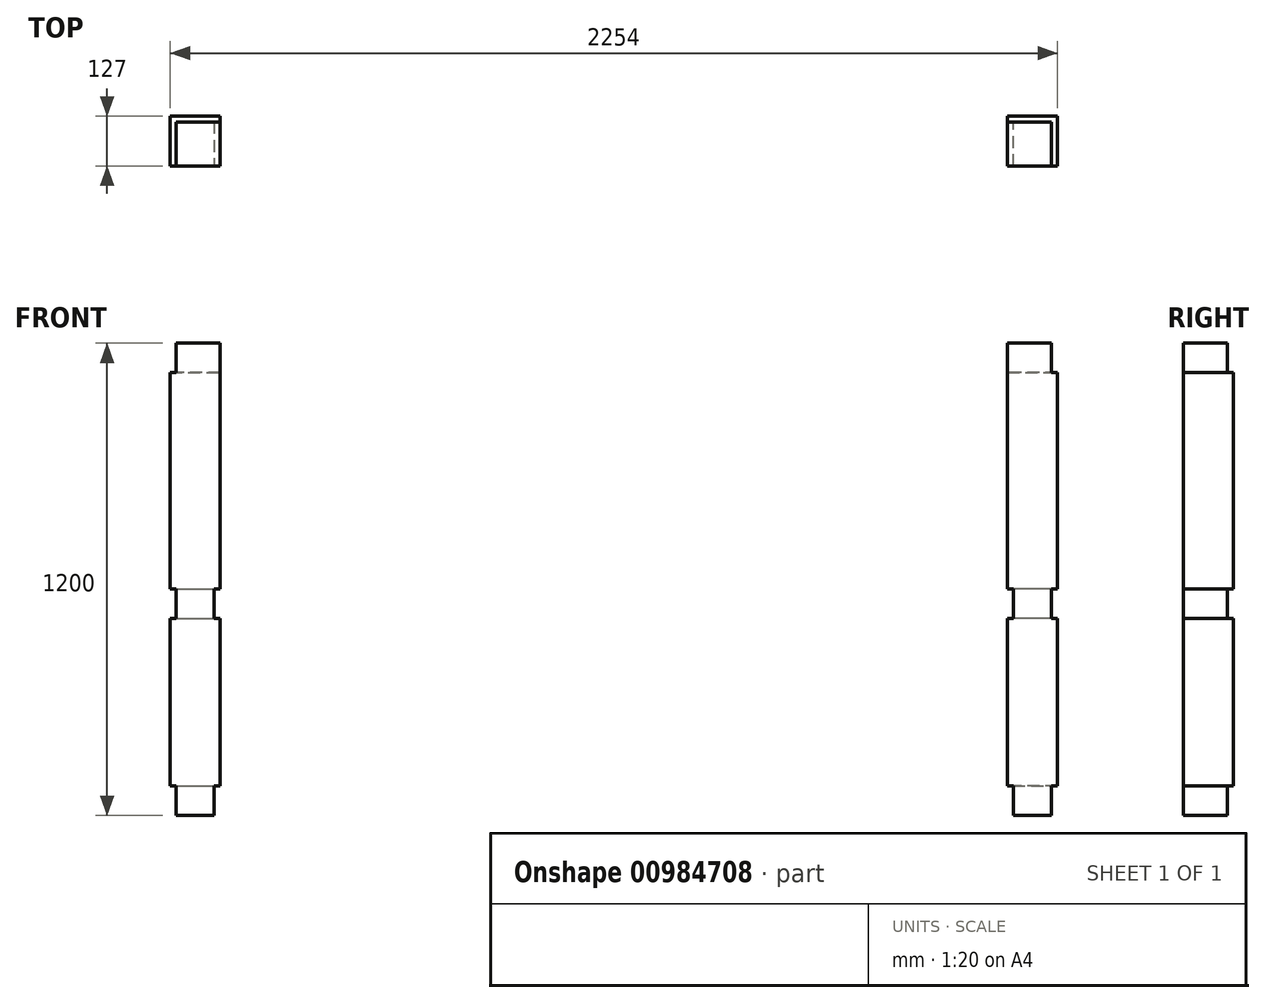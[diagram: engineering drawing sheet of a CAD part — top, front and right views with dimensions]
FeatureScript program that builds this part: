
annotation { "Feature Type Name" : "Feature", "Feature Type Description" : "" }
export const myFeature = defineFeature(function(context is Context, id is Id, definition is map)
    precondition{}
    {
        {
            var Q0;
            Q0=qCreatedBy(makeId("Top.planeOp"),FACE);
            var sketch = newSketch(context, id + "F0", { "sketchPlane" : qUnion([Q0])});
            skLineSegment(sketch, "E0.bottom", {"start": v(0, 0) * mm, "end": v(127, 0) * mm});
            skLineSegment(sketch, "E0.top", {"start": v(0, 127) * mm, "end": v(127, 127) * mm});
            skLineSegment(sketch, "E0.left", {"start": v(0, 0) * mm, "end": v(0, 127) * mm});
            skLineSegment(sketch, "E0.right", {"start": v(127, 0) * mm, "end": v(127, 127) * mm});
            skSolve(sketch);
        }
        {
            var Q0;
            Q0=qSketchRegion(id+"F0",true);
            extrude(context, id + "F1", {"entities" : qUnion([Q0]), "depth" : 1200 * mm, "offsetDistance" : 25.4 * mm});
        }
        {
            var Q0;
            Q0=makeQuery(id+"F1.opExtrude","CAP_FACE",FACE,{"disambiguationData":[OSD([sQuery(id+"F0.wireOp",EDGE,"E0.bottom"),sQuery(id+"F0.wireOp",EDGE,"E0.top"),sQuery(id+"F0.wireOp",EDGE,"E0.left"),sQuery(id+"F0.wireOp",EDGE,"E0.right")])],"isStart":false});
            var sketch = newSketch(context, id + "F2", { "sketchPlane" : qUnion([Q0])});
            skLineSegment(sketch, "E1", {"start": v(0, 0) * mm, "end": v(0, 127) * mm});
            skLineSegment(sketch, "E2", {"start": v(0, 127) * mm, "end": v(127, 127) * mm});
            skLineSegment(sketch, "E3", {"start": v(127, 127) * mm, "end": v(127, 112) * mm});
            skLineSegment(sketch, "E4", {"start": v(127, 112) * mm, "end": v(15, 112) * mm});
            skLineSegment(sketch, "E5", {"start": v(15, 112) * mm, "end": v(15, 0) * mm});
            skLineSegment(sketch, "E6", {"start": v(15, 0) * mm, "end": v(0, 0) * mm});
            skSolve(sketch);
        }
        {
            var Q0;
            Q0=qSketchRegion(id+"F2",true);
            extrude(context, id + "F3", {"entities" : qUnion([Q0]), "operationType" : NewBodyOperationType.REMOVE, "oppositeDirection" : true, "depth" : 75 * mm, "offsetDistance" : 25.4 * mm});
        }
        {
            var Q0;
            Q0=makeQuery(id+"F1.opExtrude","CAP_FACE",FACE,{"disambiguationData":[OSD([sQuery(id+"F0.wireOp",EDGE,"E0.bottom"),sQuery(id+"F0.wireOp",EDGE,"E0.top"),sQuery(id+"F0.wireOp",EDGE,"E0.left"),sQuery(id+"F0.wireOp",EDGE,"E0.right")])],"isStart":true});
            var sketch = newSketch(context, id + "F4", { "sketchPlane" : qUnion([Q0])});
            skLineSegment(sketch, "E7", {"start": v(0, 0) * mm, "end": v(15, 0) * mm});
            skLineSegment(sketch, "E8", {"start": v(15, 0) * mm, "end": v(15, -112) * mm});
            skLineSegment(sketch, "E9", {"start": v(15, -112) * mm, "end": v(112, -112) * mm});
            skLineSegment(sketch, "E10", {"start": v(112, -112) * mm, "end": v(112, 0) * mm});
            skLineSegment(sketch, "E11", {"start": v(112, 0) * mm, "end": v(127, 0) * mm});
            skLineSegment(sketch, "E12", {"start": v(127, 0) * mm, "end": v(127, -127) * mm});
            skLineSegment(sketch, "E13", {"start": v(127, -127) * mm, "end": v(0, -127) * mm});
            skLineSegment(sketch, "E14", {"start": v(0, -127) * mm, "end": v(0, 0) * mm});
            skSolve(sketch);
        }
        {
            var Q0;
            Q0=qSketchRegion(id+"F4",true);
            extrude(context, id + "F5", {"entities" : qUnion([Q0]), "operationType" : NewBodyOperationType.REMOVE, "oppositeDirection" : true, "depth" : 575 * mm, "offsetDistance" : 25.4 * mm, "hasSecondDirection" : true, "secondDirectionOppositeDirection" : true, "secondDirectionDepth" : 500 * mm});
        }
        {
            var Q0;
            Q0=qCreatedBy(makeId("Right.planeOp"),FACE);
            cPlane(context, id + "F6", {"entities" : qUnion([Q0]), "cplaneType" : CPlaneType.OFFSET, "offset" : 1127 * mm, "width" : 152.4 * mm, "height" : 152.4 * mm});
        }
        {
            var Q0;
            Q0=makeQuery(id+"F1.opExtrude","SWEPT_BODY",BODY,{"disambiguationData":[OSD([sQuery(id+"F0.wireOp",EDGE,"E0.bottom"),sQuery(id+"F0.wireOp",EDGE,"E0.top"),sQuery(id+"F0.wireOp",EDGE,"E0.left"),sQuery(id+"F0.wireOp",EDGE,"E0.right")])]});
            var Q1;
            Q1=qCreatedBy(id+"F6.planeOp",FACE);
            mirror(context, id + "F7", {"entities" : qUnion([Q0]), "mirrorPlane" : qUnion([Q1])});
        }
        {
            var Q0;
            Q0=makeQuery(id+"F7.opPattern","COPY",FACE,{"derivedFrom":makeQuery(id+"F1.opExtrude","CAP_FACE",FACE,{"disambiguationData":[OSD([sQuery(id+"F0.wireOp",EDGE,"E0.bottom"),sQuery(id+"F0.wireOp",EDGE,"E0.top"),sQuery(id+"F0.wireOp",EDGE,"E0.left"),sQuery(id+"F0.wireOp",EDGE,"E0.right")])],"isStart":true}),"instanceName":"1"});
            var sketch = newSketch(context, id + "F8", { "sketchPlane" : qUnion([Q0])});
            skLineSegment(sketch, "E15", {"start": v(2254, 0) * mm, "end": v(2254, -127) * mm});
            skLineSegment(sketch, "E16", {"start": v(2254, -127) * mm, "end": v(2127, -127) * mm});
            skLineSegment(sketch, "E17", {"start": v(2127, -127) * mm, "end": v(2127, 0) * mm});
            skLineSegment(sketch, "E18", {"start": v(2127, 0) * mm, "end": v(2142, 0) * mm});
            skLineSegment(sketch, "E19", {"start": v(2142, 0) * mm, "end": v(2142, -112) * mm});
            skLineSegment(sketch, "E20", {"start": v(2142, -112) * mm, "end": v(2239, -112) * mm});
            skLineSegment(sketch, "E21", {"start": v(2239, -112) * mm, "end": v(2239, 0) * mm});
            skLineSegment(sketch, "E22", {"start": v(2239, 0) * mm, "end": v(2254, 0) * mm});
            skSolve(sketch);
        }
        {
            var Q0;
            Q0=makeQuery(id+"F8.imprint","IMPRINT",FACE,{"disambiguationData":[TD([[makeQuery(id+"F8.imprint","IMPRINT",EDGE,{"derivedFrom":sQuery(id+"F8.wireOp",EDGE,"E15")}),-1.0]])]});
            extrude(context, id + "F9", {"entities" : qUnion([Q0]), "operationType" : NewBodyOperationType.REMOVE, "oppositeDirection" : true, "depth" : 75 * mm, "offsetDistance" : 25.4 * mm});
        }
        {
            var Q0;
            Q0=makeQuery(id+"F1.opExtrude","CAP_FACE",FACE,{"disambiguationData":[OSD([sQuery(id+"F0.wireOp",EDGE,"E0.bottom"),sQuery(id+"F0.wireOp",EDGE,"E0.top"),sQuery(id+"F0.wireOp",EDGE,"E0.left"),sQuery(id+"F0.wireOp",EDGE,"E0.right")])],"isStart":true});
            var sketch = newSketch(context, id + "F10", { "sketchPlane" : qUnion([Q0])});
            skLineSegment(sketch, "E23", {"start": v(127, 0) * mm, "end": v(127, -127) * mm});
            skLineSegment(sketch, "E24", {"start": v(127, -127) * mm, "end": v(0, -127) * mm});
            skLineSegment(sketch, "E25", {"start": v(0, -127) * mm, "end": v(0, 0) * mm});
            skLineSegment(sketch, "E26", {"start": v(0, 0) * mm, "end": v(15, 0) * mm});
            skLineSegment(sketch, "E27", {"start": v(15, 0) * mm, "end": v(15, -112) * mm});
            skLineSegment(sketch, "E28", {"start": v(15, -112) * mm, "end": v(112, -112) * mm});
            skLineSegment(sketch, "E29", {"start": v(112, -112) * mm, "end": v(112, 0) * mm});
            skLineSegment(sketch, "E30", {"start": v(112, 0) * mm, "end": v(127, 0) * mm});
            skSolve(sketch);
        }
        {
            var Q0;
            Q0=makeQuery(id+"F10.imprint","IMPRINT",FACE,{"disambiguationData":[TD([[makeQuery(id+"F10.imprint","IMPRINT",EDGE,{"derivedFrom":sQuery(id+"F10.wireOp",EDGE,"E23")}),-1.0]])]});
            extrude(context, id + "F11", {"entities" : qUnion([Q0]), "operationType" : NewBodyOperationType.REMOVE, "oppositeDirection" : true, "depth" : 75 * mm, "offsetDistance" : 25.4 * mm});
        }
    });
